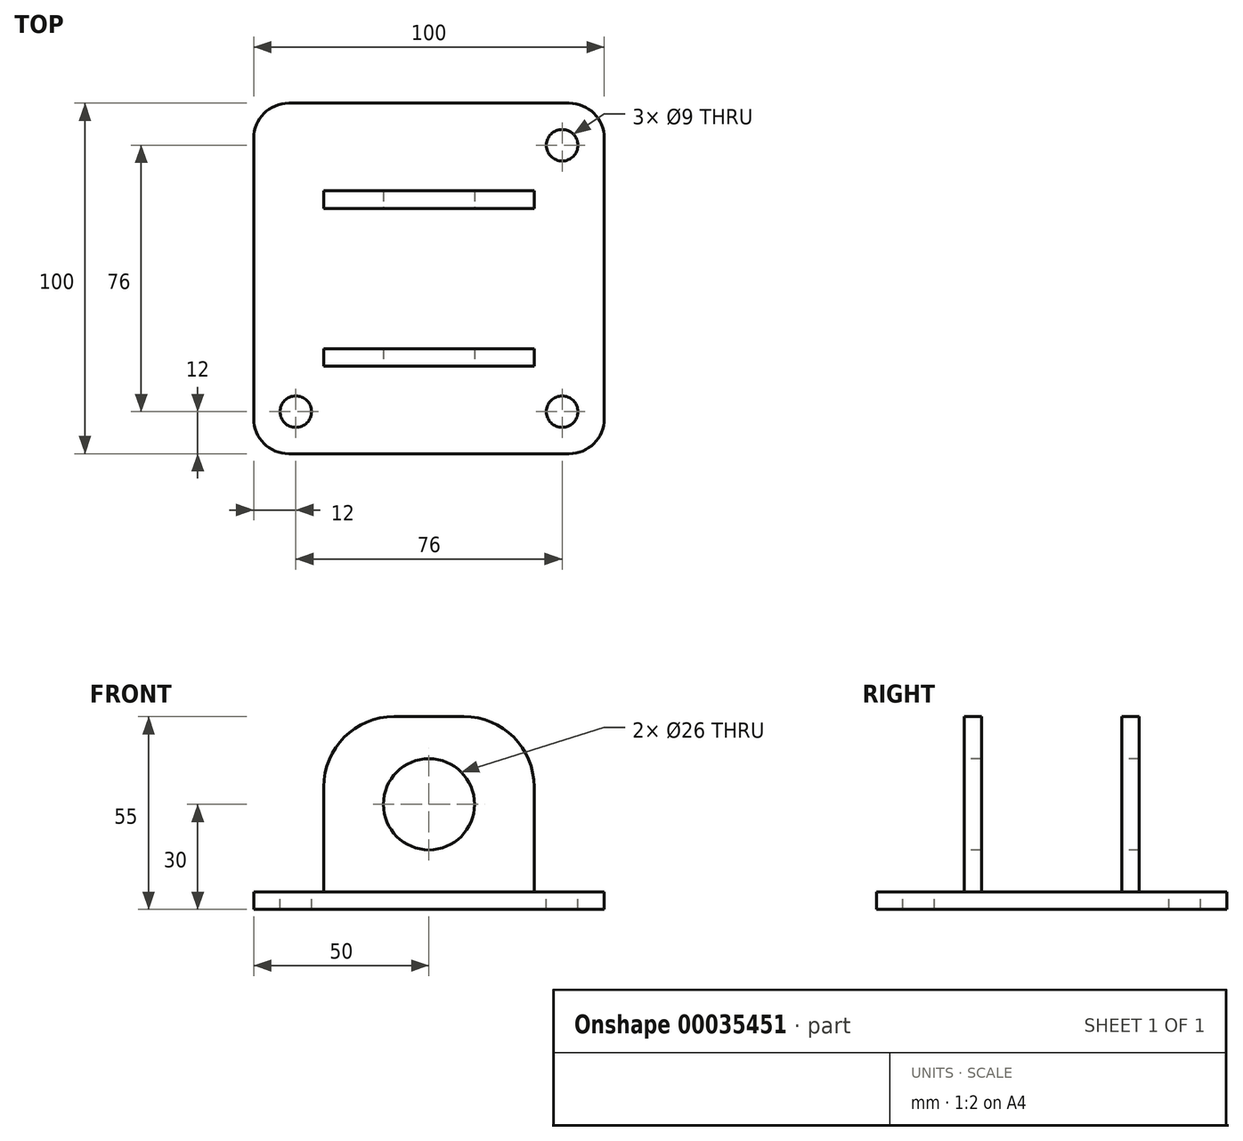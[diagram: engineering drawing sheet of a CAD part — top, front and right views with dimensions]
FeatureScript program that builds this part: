
annotation { "Feature Type Name" : "Feature", "Feature Type Description" : "" }
export const myFeature = defineFeature(function(context is Context, id is Id, definition is map)
    precondition{}
    {
        {
            assignVariable(context, id + "F0", {"name" : "x", "anyValue" : 5});
        }
        {
            var Q0;
            Q0=qCreatedBy(makeId("Top.planeOp"),FACE);
            var sketch = newSketch(context, id + "F1", { "sketchPlane" : qUnion([Q0])});
            skLineSegment(sketch, "E0.bottom", {"start": v(-50, -50) * mm, "end": v(50, -50) * mm});
            skLineSegment(sketch, "E0.top", {"start": v(-50, 50) * mm, "end": v(50, 50) * mm});
            skLineSegment(sketch, "E0.left", {"start": v(-50, -50) * mm, "end": v(-50, 50) * mm});
            skLineSegment(sketch, "E0.right", {"start": v(50, -50) * mm, "end": v(50, 50) * mm});
            skLineSegment(sketch, "E1", {"start": v(0, 50) * mm, "end": v(0, -50) * mm, "construction": true});
            skLineSegment(sketch, "E2", {"start": v(-50, 0) * mm, "end": v(50, 0) * mm, "construction": true});
            skSolve(sketch);
        }
        {
            var Q0;
            Q0=makeQuery(id+"F1.imprint","IMPRINT",FACE,{"disambiguationData":[TD([[makeQuery(id+"F1.imprint","IMPRINT",EDGE,{"derivedFrom":sQuery(id+"F1.wireOp",EDGE,"E0.bottom")}),1.0]])]});
            extrude(context, id + "F2", {"entities" : qUnion([Q0]), "depth" : (getVariable(context, 'x')) * mm});
        }
        {
            var Q0;
            Q0=makeQuery(id+"F2.opExtrude","SWEPT_EDGE",EDGE,{"disambiguationData":[OSD([sQuery(id+"F1.wireOp",EDGE,"E0.top"),sQuery(id+"F1.wireOp",EDGE,"E0.left")])]});
            var Q1;
            Q1=makeQuery(id+"F2.opExtrude","SWEPT_EDGE",EDGE,{"disambiguationData":[OSD([sQuery(id+"F1.wireOp",EDGE,"E0.bottom"),sQuery(id+"F1.wireOp",EDGE,"E0.left")])]});
            var Q2;
            Q2=makeQuery(id+"F2.opExtrude","SWEPT_EDGE",EDGE,{"disambiguationData":[OSD([sQuery(id+"F1.wireOp",EDGE,"E0.bottom"),sQuery(id+"F1.wireOp",EDGE,"E0.right")])]});
            var Q3;
            Q3=makeQuery(id+"F2.opExtrude","SWEPT_EDGE",EDGE,{"disambiguationData":[OSD([sQuery(id+"F1.wireOp",EDGE,"E0.top"),sQuery(id+"F1.wireOp",EDGE,"E0.right")])]});
            fillet(context, id + "F3", {"entities" : qUnion([Q0, Q1, Q2, Q3]), "radius" : (2 * getVariable(context, 'x')) * mm, "tangentPropagation" : true, "allowEdgeOverflow" : false});
        }
        {
            var Q0;
            Q0=makeQuery(id+"F2.opExtrude","CAP_FACE",FACE,{"disambiguationData":[OSD([sQuery(id+"F1.wireOp",EDGE,"E0.bottom"),sQuery(id+"F1.wireOp",EDGE,"E0.top"),sQuery(id+"F1.wireOp",EDGE,"E0.left"),sQuery(id+"F1.wireOp",EDGE,"E0.right")])],"isStart":false});
            var sketch = newSketch(context, id + "F4", { "sketchPlane" : qUnion([Q0])});
            skLineSegment(sketch, "E3.bottom", {"start": v(-38, -38) * mm, "end": v(38, -38) * mm, "construction": true});
            skLineSegment(sketch, "E3.top", {"start": v(-38, 38) * mm, "end": v(38, 38) * mm, "construction": true});
            skLineSegment(sketch, "E3.left", {"start": v(-38, 38) * mm, "end": v(-38, -38) * mm, "construction": true});
            skLineSegment(sketch, "E3.right", {"start": v(38, 38) * mm, "end": v(38, -38) * mm, "construction": true});
            skSolve(sketch);
        }
        {
            var Q0;
            Q0=sQuery(id+"F4.wireOp",VERTEX,"E3.left.end");
            var Q1;
            Q1=sQuery(id+"F4.wireOp",VERTEX,"E3.right.end");
            var Q2;
            Q2=sQuery(id+"F4.wireOp",VERTEX,"E3.bottom.start");
            var Q3;
            Q3=sQuery(id+"F4.wireOp",VERTEX,"E3.right.start");
            var Q4;
            Q4=makeQuery(id+"F2.opExtrude","SWEPT_BODY",BODY,{"disambiguationData":[OSD([sQuery(id+"F1.wireOp",EDGE,"E0.bottom"),sQuery(id+"F1.wireOp",EDGE,"E0.top"),sQuery(id+"F1.wireOp",EDGE,"E0.left"),sQuery(id+"F1.wireOp",EDGE,"E0.right")])]});
            hole(context, id + "F5", {"style" : HoleStyle.SIMPLE, "holeDiameter" : 9 * mm, "endStyle" : HoleEndStyle.THROUGH, "locations" : qUnion([Q0, Q1, Q2, Q3]), "scope" : qUnion([Q4])});
        }
        {
            var Q0;
            Q0=makeQuery(id+"F2.opExtrude","CAP_FACE",FACE,{"disambiguationData":[OSD([sQuery(id+"F1.wireOp",EDGE,"E0.bottom"),sQuery(id+"F1.wireOp",EDGE,"E0.top"),sQuery(id+"F1.wireOp",EDGE,"E0.left"),sQuery(id+"F1.wireOp",EDGE,"E0.right")])],"isStart":false});
            var sketch = newSketch(context, id + "F6", { "sketchPlane" : qUnion([Q0])});
            skLineSegment(sketch, "E4.bottom", {"start": v(-30, -25) * mm, "end": v(30, -25) * mm});
            skLineSegment(sketch, "E4.top", {"start": v(-30, -20) * mm, "end": v(30, -20) * mm});
            skLineSegment(sketch, "E4.left", {"start": v(-30, -25) * mm, "end": v(-30, -20) * mm});
            skLineSegment(sketch, "E4.right", {"start": v(30, -25) * mm, "end": v(30, -20) * mm});
            skLineSegment(sketch, "E5.MirrorCS", {"start": v(-30, 25) * mm, "end": v(-30, 20) * mm});
            skLineSegment(sketch, "E6.MirrorCS", {"start": v(30, 25) * mm, "end": v(30, 20) * mm});
            skLineSegment(sketch, "E7.MirrorCS", {"start": v(-30, 25) * mm, "end": v(30, 25) * mm});
            skLineSegment(sketch, "E8.MirrorCS", {"start": v(-30, 20) * mm, "end": v(30, 20) * mm});
            skSolve(sketch);
        }
        {
            var Q0;
            Q0 = qSketchRegion(id + "F6", true);
            extrude(context, id + "F7", {"entities" : qUnion([Q0]), "operationType" : NewBodyOperationType.ADD, "depth" : 50 * mm});
        }
        {
            var Q0;
            Q0=makeQuery(id+"F7.opExtrude","CAP_EDGE",EDGE,{"disambiguationData":[OSD([sQuery(id+"F6.wireOp",EDGE,"E4.left")])],"isStart":false});
            var Q1;
            Q1=makeQuery(id+"F7.opExtrude","CAP_EDGE",EDGE,{"disambiguationData":[OSD([sQuery(id+"F6.wireOp",EDGE,"E5.MirrorCS")])],"isStart":false});
            var Q2;
            Q2=makeQuery(id+"F7.opExtrude","CAP_EDGE",EDGE,{"disambiguationData":[OSD([sQuery(id+"F6.wireOp",EDGE,"E6.MirrorCS")])],"isStart":false});
            var Q3;
            Q3=makeQuery(id+"F7.opExtrude","CAP_EDGE",EDGE,{"disambiguationData":[OSD([sQuery(id+"F6.wireOp",EDGE,"E4.right")])],"isStart":false});
            fillet(context, id + "F8", {"entities" : qUnion([Q0, Q1, Q2, Q3]), "radius" : (4 * getVariable(context, 'x')) * mm, "tangentPropagation" : true, "allowEdgeOverflow" : false});
        }
        {
            var Q0;
            Q0=makeQuery(id+"F7.opExtrude","SWEPT_FACE",FACE,{"disambiguationData":[OSD([sQuery(id+"F6.wireOp",EDGE,"E4.bottom")])]});
            var sketch = newSketch(context, id + "F9", { "sketchPlane" : qUnion([Q0])});
            skLineSegment(sketch, "E9", {"start": v(0, 55) * mm, "end": v(0, 5) * mm, "construction": true});
            skLineSegment(sketch, "E10", {"start": v(30, 30) * mm, "end": v(-30, 30) * mm, "construction": true});
            skPoint(sketch, "E10.startSnap0", {"position": v(0, 30) * mm});
            skSolve(sketch);
        }
        {
            var Q0;
            Q0=sQuery(id+"F9.wireOp",VERTEX,"E10.startSnap0");
            var Q1;
            Q1=makeQuery(id+"F2.opExtrude","SWEPT_BODY",BODY,{"disambiguationData":[OSD([sQuery(id+"F1.wireOp",EDGE,"E0.bottom"),sQuery(id+"F1.wireOp",EDGE,"E0.top"),sQuery(id+"F1.wireOp",EDGE,"E0.left"),sQuery(id+"F1.wireOp",EDGE,"E0.right")])]});
            hole(context, id + "F10", {"style" : HoleStyle.SIMPLE, "holeDiameter" : (5 * getVariable(context, 'x') + 1) * mm, "endStyle" : HoleEndStyle.THROUGH, "locations" : qUnion([Q0]), "scope" : qUnion([Q1])});
        }
    });
